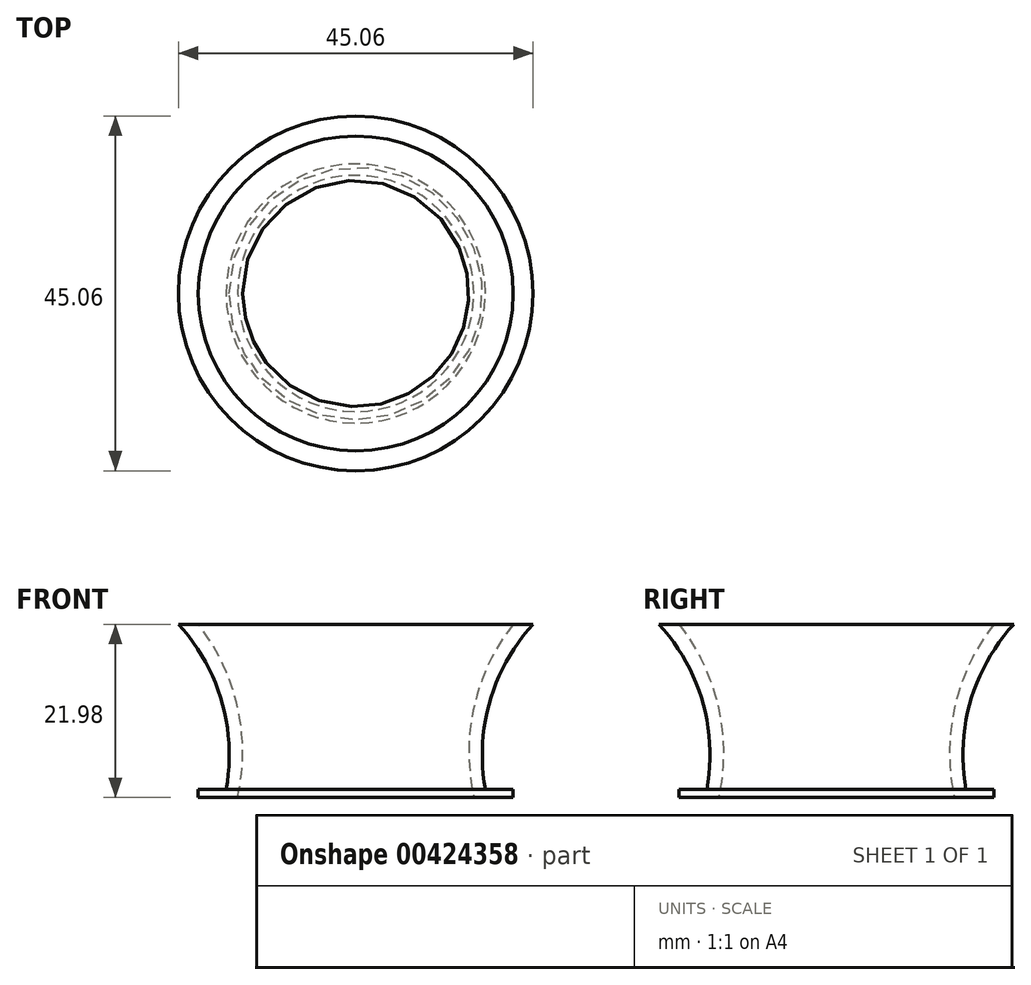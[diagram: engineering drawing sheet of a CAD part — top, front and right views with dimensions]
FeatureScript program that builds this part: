
annotation { "Feature Type Name" : "Feature", "Feature Type Description" : "" }
export const myFeature = defineFeature(function(context is Context, id is Id, definition is map)
    precondition{}
    {
        {
            var Q0;
            Q0=qCreatedBy(makeId("Front.planeOp"),FACE);
            var sketch = newSketch(context, id + "F0", { "sketchPlane" : qUnion([Q0])});
            skLineSegment(sketch, "E0", {"start": v(-5, 1) * mm, "end": v(-5, 0) * mm});
            skLineSegment(sketch, "E1", {"start": v(-5, 0) * mm, "end": v(0, 0) * mm});
            skLineSegment(sketch, "E2", {"start": v(0, 0) * mm, "end": v(0, 0) * mm});
            skLineSegment(sketch, "E3", {"start": v(8.84, -17.89) * mm, "end": v(8.84, -17.89) * mm});
            skLineSegment(sketch, "E4", {"start": v(15, 0) * mm, "end": v(15, 21.98) * mm});
            skLineSegment(sketch, "E5", {"start": v(-1.47, 1) * mm, "end": v(-5, 1) * mm});
            skArc(sketch, "E6", {"start": v(-1.47, 1) * mm, "mid": v(-2.03, 12.2) * mm, "end": v(-7.53, 21.98) * mm});
            skArc(sketch, "E7", {"start": v(0, 0) * mm, "mid": v(-0.03, 11.55) * mm, "end": v(-5, 21.98) * mm});
            skLineSegment(sketch, "E8", {"start": v(-5, 21.98) * mm, "end": v(-7.53, 21.98) * mm});
            skSolve(sketch);
        }
        {
            var Q0;
            Q0=makeQuery(id+"F0.imprint","IMPRINT",FACE,{"disambiguationData":[TD([[makeQuery(id+"F0.imprint","IMPRINT",EDGE,{"derivedFrom":sQuery(id+"F0.wireOp",EDGE,"E0")}),1.0]])]});
            var Q1;
            Q1=sQuery(id+"F0.wireOp",EDGE,"E4");
            revolve(context, id + "F1", {"entities" : qUnion([Q0]), "axis" : qUnion([Q1]), "revolveType" : RevolveType.FULL});
        }
    });
